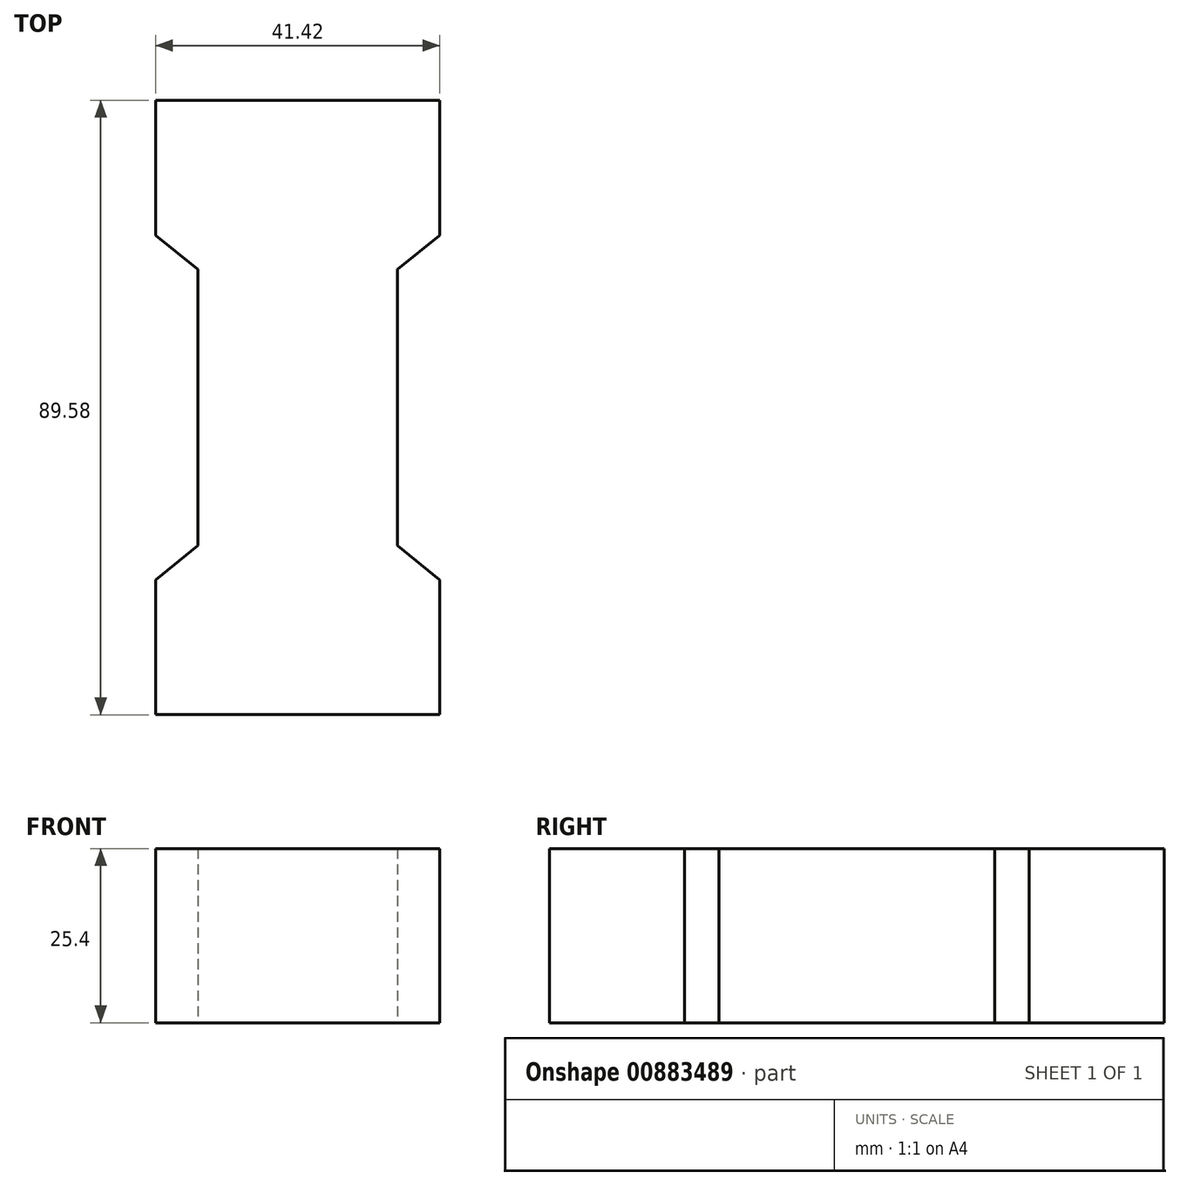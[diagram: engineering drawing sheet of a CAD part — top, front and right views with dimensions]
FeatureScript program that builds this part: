
annotation { "Feature Type Name" : "Feature", "Feature Type Description" : "" }
export const myFeature = defineFeature(function(context is Context, id is Id, definition is map)
    precondition{}
    {
        {
            var Q0;
            Q0=qCreatedBy(makeId("Top.planeOp"),FACE);
            var sketch = newSketch(context, id + "F0", { "sketchPlane" : qUnion([Q0])});
            skLineSegment(sketch, "E0", {"start": v(0, 0) * mm, "end": v(-14.54, 0) * mm});
            skLineSegment(sketch, "E1", {"start": v(-14.54, 0) * mm, "end": v(-14.54, 20.12) * mm});
            skLineSegment(sketch, "E2", {"start": v(-14.54, 20.12) * mm, "end": v(-20.7, 25.11) * mm});
            skLineSegment(sketch, "E3", {"start": v(-20.7, 25.11) * mm, "end": v(-20.7, 44.79) * mm});
            skLineSegment(sketch, "E4", {"start": v(-20.7, 44.79) * mm, "end": v(0, 44.79) * mm});
            skLineSegment(sketch, "E5.MirrorCS", {"start": v(14.54, 0) * mm, "end": v(14.54, 20.12) * mm});
            skLineSegment(sketch, "E6.MirrorCS", {"start": v(14.54, 20.12) * mm, "end": v(20.7, 25.11) * mm});
            skLineSegment(sketch, "E7.MirrorCS", {"start": v(20.7, 44.79) * mm, "end": v(0, 44.79) * mm});
            skLineSegment(sketch, "E8.MirrorCS", {"start": v(20.7, 25.11) * mm, "end": v(20.7, 44.79) * mm});
            skLineSegment(sketch, "E9.MirrorCS", {"start": v(-20.7, -44.79) * mm, "end": v(0, -44.79) * mm});
            skLineSegment(sketch, "E10.MirrorCS", {"start": v(20.7, -44.79) * mm, "end": v(0, -44.79) * mm});
            skLineSegment(sketch, "E11.MirrorCS", {"start": v(20.7, -25.11) * mm, "end": v(20.7, -44.79) * mm});
            skLineSegment(sketch, "E12.MirrorCS", {"start": v(14.54, -20.12) * mm, "end": v(20.7, -25.11) * mm});
            skLineSegment(sketch, "E13.MirrorCS", {"start": v(14.54, 0) * mm, "end": v(14.54, -20.12) * mm});
            skLineSegment(sketch, "E14.MirrorCS", {"start": v(-14.54, 0) * mm, "end": v(-14.54, -20.12) * mm});
            skLineSegment(sketch, "E15.MirrorCS", {"start": v(-14.54, -20.12) * mm, "end": v(-20.7, -25.11) * mm});
            skLineSegment(sketch, "E16.MirrorCS", {"start": v(-20.7, -25.11) * mm, "end": v(-20.7, -44.79) * mm});
            skSolve(sketch);
        }
        {
            var Q0;
            Q0 = qSketchRegion(id + "F0", true);
            extrude(context, id + "F1", {"entities" : qUnion([Q0]), "depth" : 25.4 * mm, "offsetDistance" : 25.4 * mm});
        }
    });
